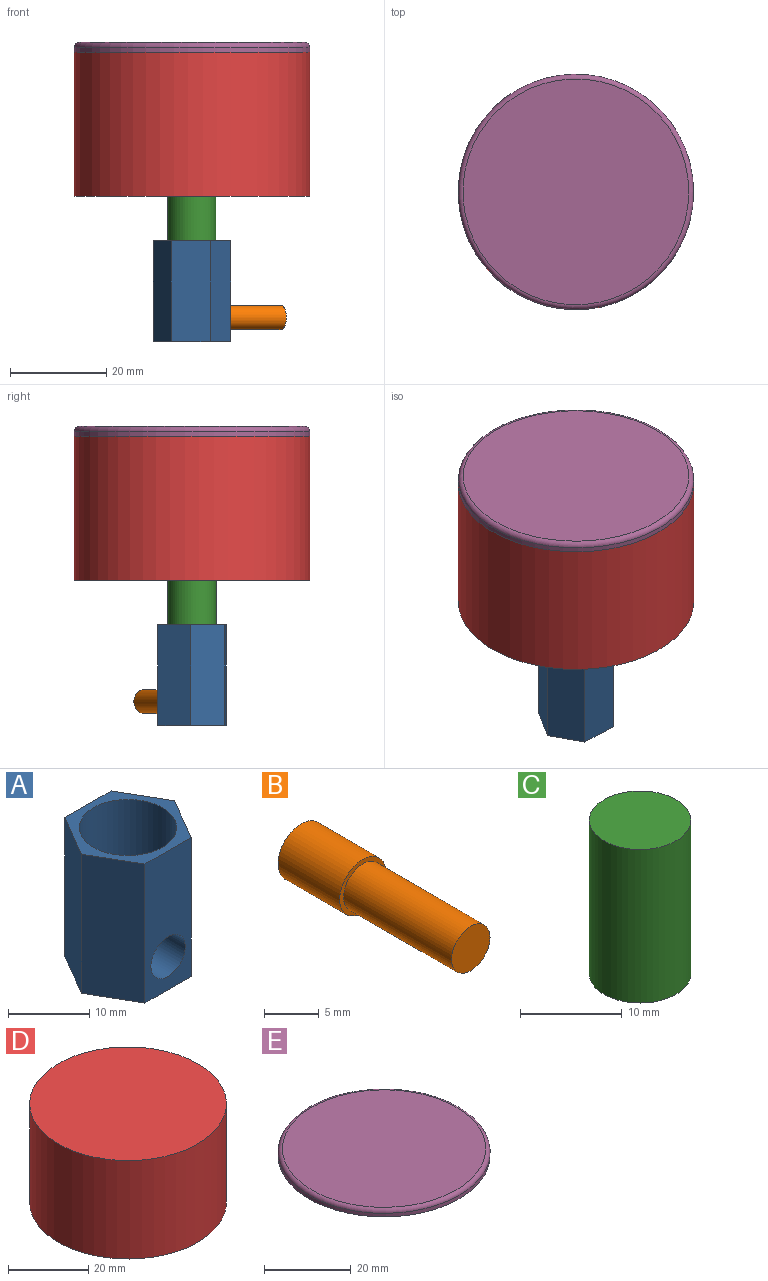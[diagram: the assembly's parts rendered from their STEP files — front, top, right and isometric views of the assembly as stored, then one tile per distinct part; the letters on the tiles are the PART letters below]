
ASSEMBLY  parts=5 mates=4
PART A: 16 faces, bbox 16.2x14x21 mm
  f0: plane 21x8.08mm, normal (0,1,0), area 169.7mm2, adj f1,f5,f6,f7
  f1: plane 21x7mm, normal (-0.87,0.5,0), area 169.7mm2, adj f0,f2,f6,f7
  f2: plane 21x7mm, normal (-0.87,-0.5,0), area 169.7mm2, adj f1,f3,f6,f7
  f3: plane 21x8.08mm, normal (0,-1,0), area 141.5mm2, adj f2,f4,f6,f7,f13
  f4: plane 21x7mm, normal (0.87,-0.5,0), area 169.7mm2, adj f3,f5,f6,f7
  f5: plane 21x7mm, normal (0.87,0.5,0), area 169.7mm2, adj f0,f4,f6,f7
  f6: plane 16.17x14mm, normal (0,0,1), area 56.6mm2, adj f0,f1,f2,f3,f4,f5,f8
  f7: plane 16.17x14mm, normal (0,0,-1), area 169.7mm2, adj f0,f1,f2,f3,f4,f5
  f8: cylinder r=6mm len=12mm, axis (0,0,1), area 377mm2, adj f6,f9
  f9: plane 12x12mm, normal (0,0,1), area 93.5mm2, adj f8,f10
  f10: cylinder r=2.5mm len=9mm, axis (0,0,1), area 101.6mm2, adj f9,f11,f12,f13,f14,f15
  f11: cylinder r=2.5mm len=2.5mm, axis (0,0,1), area 2.4mm2, adj f10,f12,f13
  f12: plane 5x5mm, normal (0,0,1), area 19.6mm2, adj f10,f11
  f13: cylinder r=3mm len=7mm, axis (0,-1,0), area 109.9mm2, adj f3,f10,f11,f14,f15
  f14: plane 3.32x0.5mm, normal (0,-1,0), area 1.1mm2, adj f10,f13
  f15: plane 3.32x0.5mm, normal (0,-1,0), area 1.1mm2, adj f10,f13
PART B: 5 faces, bbox 6x22x6 mm
  f0: cylinder r=3mm len=8mm, axis (0,1,0), area 150.8mm2, adj f1,f2
  f1: plane 6x6mm, normal (0,-1,0), area 8.6mm2, adj f0,f3
  f2: plane 6x6mm, normal (0,1,0), area 28.3mm2, adj f0
  f3: cylinder r=2.5mm len=14mm, axis (0,1,0), area 219.9mm2, adj f1,f4
  f4: plane 5x5mm, normal (0,-1,0), area 19.6mm2, adj f3
PART C: 3 faces, bbox 10x10x18.5 mm
  f0: cylinder r=5mm len=18.5mm, axis (0,0,1), area 581.2mm2, adj f1,f2
  f1: plane 10x10mm, normal (0,0,-1), area 78.5mm2, adj f0
  f2: plane 10x10mm, normal (0,0,1), area 78.5mm2, adj f0
PART D: 3 faces, bbox 49x49x30 mm
  f0: cylinder r=24.5mm len=49mm, axis (0,0,-1), area 4618.1mm2, adj f1,f2
  f1: plane 49x49mm, normal (0,0,1), area 1885.7mm2, adj f0
  f2: plane 49x49mm, normal (0,0,-1), area 1885.7mm2, adj f0
PART E: 4 faces, bbox 53x53x2 mm
  f0: cylinder r=24.5mm len=49mm, axis (0,0,-1), area 153.9mm2, adj f2,f3
  f1: plane 47x47mm, normal (0,0,1), area 1734.9mm2, adj f3
  f2: plane 49x49mm, normal (0,0,-1), area 1885.7mm2, adj f0
  f3: torus R=23.5mm, axis (0,0,1), area 238.2mm2, adj f0,f1
PLACE A rot(axis=(0,0,1),118.2deg) t=(0,0,24.75)mm
PLACE B rot(axis=(0,0,1),118.2deg) t=(-22.92,-12.27,12.67)mm
PLACE C at identity
PLACE D at identity
PLACE E at identity
MATE fastened E.f0 <-> D.f0  axis (0,0,-1) through (0,0,30)mm
MATE fastened C.f0 <-> D.f0  axis (0,0,1) through (0,0,0)mm
MATE revolute A.f8 <-> C.f0  axis (0,0,1) through (0,0,-9.25)mm
MATE fastened B.f0 <-> A.f13  axis (0.88,0.47,0) through (6.17,3.3,-25.25)mm
